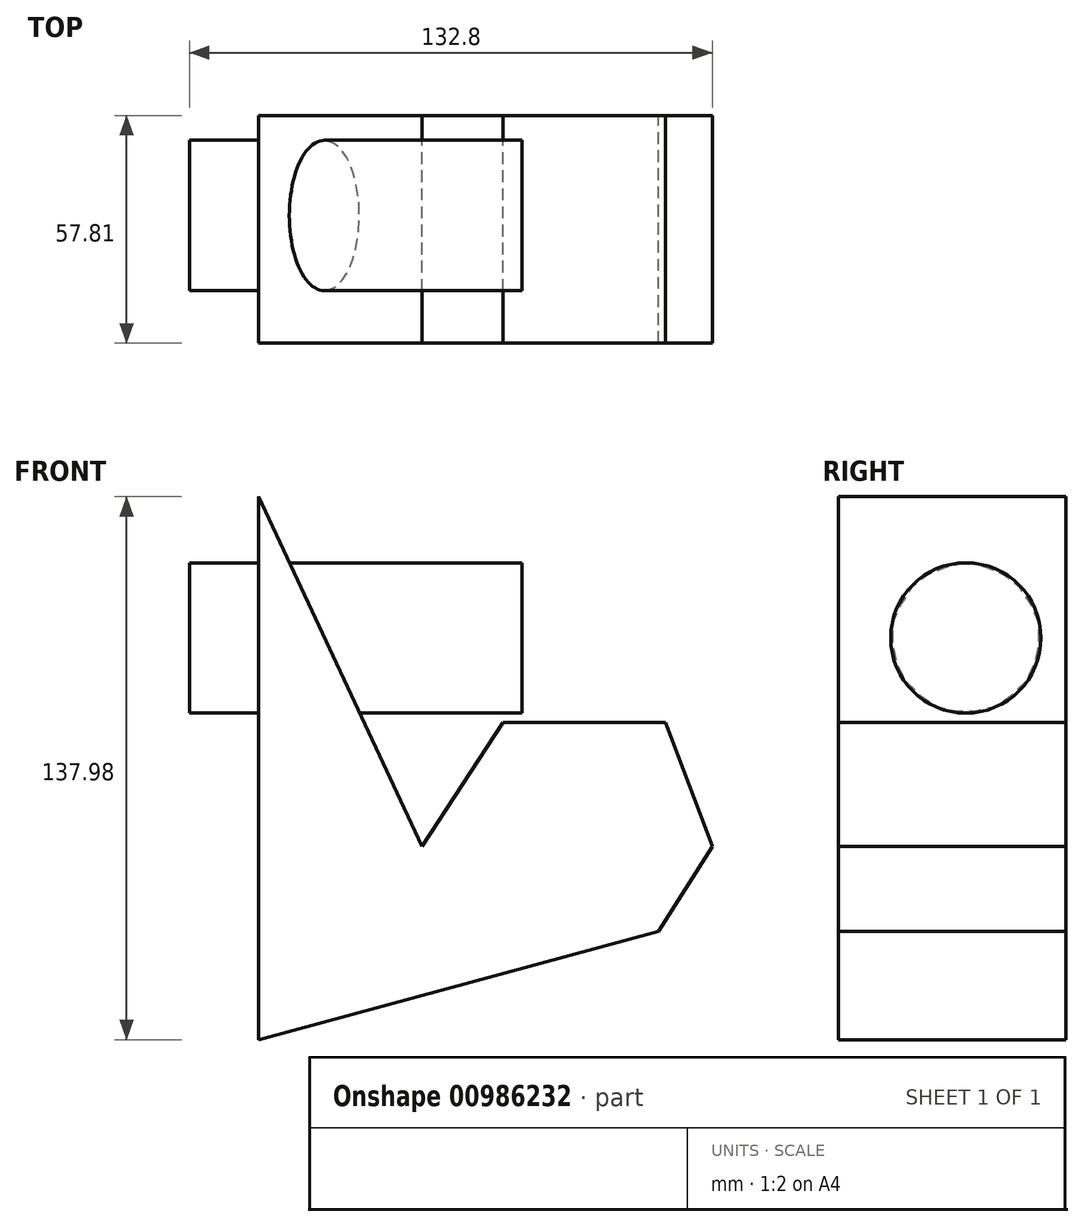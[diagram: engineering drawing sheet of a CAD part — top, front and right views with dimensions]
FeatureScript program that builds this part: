
annotation { "Feature Type Name" : "Feature", "Feature Type Description" : "" }
export const myFeature = defineFeature(function(context is Context, id is Id, definition is map)
    precondition{}
    {
        {
            var Q0;
            Q0=qCreatedBy(makeId("Front.planeOp"),FACE);
            var sketch = newSketch(context, id + "F0", { "sketchPlane" : qUnion([Q0])});
            skLineSegment(sketch, "E0", {"start": v(0, 0) * mm, "end": v(20.63, 31.5) * mm});
            skLineSegment(sketch, "E1", {"start": v(20.63, 31.5) * mm, "end": v(61.91, 31.5) * mm});
            skLineSegment(sketch, "E2", {"start": v(61.91, 31.5) * mm, "end": v(73.8, 0) * mm});
            skLineSegment(sketch, "E3", {"start": v(73.8, 0) * mm, "end": v(60.16, -21.56) * mm});
            skLineSegment(sketch, "E4", {"start": v(60.16, -21.56) * mm, "end": v(-41.52, -49.08) * mm});
            skLineSegment(sketch, "E5", {"start": v(-41.52, -49.08) * mm, "end": v(-41.52, 88.9) * mm});
            skLineSegment(sketch, "E6", {"start": v(-41.52, 88.9) * mm, "end": v(0, 0) * mm});
            skSolve(sketch);
        }
        {
            var Q0;
            Q0=qCreatedBy(makeId("Right.planeOp"),FACE);
            var sketch = newSketch(context, id + "F1", { "sketchPlane" : qUnion([Q0])});
            skCircle(sketch, "E7", {"center": v(0, 52.99) * mm, "radius": 19.1 * mm});
            skSolve(sketch);
        }
        {
            var Q0;
            Q0=makeQuery(id+"F0.imprint","IMPRINT",FACE,{"disambiguationData":[TD([[makeQuery(id+"F0.imprint","IMPRINT",EDGE,{"derivedFrom":sQuery(id+"F0.wireOp",EDGE,"E0")}),-1.0]])]});
            extrude(context, id + "F2", {"entities" : qUnion([Q0]), "depth" : 32.4 * mm, "offsetDistance" : 25.4 * mm, "hasSecondDirection" : true, "secondDirectionOppositeDirection" : true, "secondDirectionDepth" : 25.4 * mm});
        }
        {
            var Q0;
            Q0=makeQuery(id+"F1.imprint","IMPRINT",FACE,{"disambiguationData":[TD([[makeQuery(id+"F1.imprint","IMPRINT",EDGE,{"derivedFrom":sQuery(id+"F1.wireOp",EDGE,"E7")}),1.0]])]});
            extrude(context, id + "F3", {"entities" : qUnion([Q0]), "operationType" : NewBodyOperationType.ADD, "depth" : 25.4 * mm, "offsetDistance" : 25.4 * mm, "hasSecondDirection" : true, "secondDirectionOppositeDirection" : true, "secondDirectionDepth" : 59 * mm});
        }
    });
